# Revit family: Sideboard-Teknion-CFBTL-Figure-36h_Triple_Low_Base-R2023
name_source: partatom
category: Furniture
units: mm (PartAtom-declared; Revit-internal decimal feet)

## family parameters
Always vertical = Yes
Cut with Voids When Loaded = No
Enable Cutting in Views = No
OmniClass Number = 23.40.20.00
OmniClass Title = General Furniture and Specialties
Render Appearance Source = Family Geometry
Room Calculation Point = No
Shared = Yes
Work Plane-Based = Yes

## types (6) — shared parameters
Assembly Code = E2020200
Default Elevation = 48 "
Description = 36H Triple Sideboard, Low Base
Dim1 = 15 "
HDH = No
Height = 37 "
Manufacturer = Teknion
Manufacturer Fax = 416.661.4586
Part Number = CFBTL
Product Documentation Link = https://d2r72yk5wmppdj.cloudfront.net
Product Line = Custom Wood
Product Page URL = https://www.teknion.com
Series = Figure
Sustainability Data = https://www.teknion.com
URL = www.teknion.com
Unit Weight URL = http://www.teknion.com
Warranty = http://www.teknion.com

## per-type parameters (varying)
| type | HCH | HHH | HWH | Model | WCW | WDW |
| (HHH) All H.Doors | No | Yes | No | CFBTL_HHH | No | No |
| (HCH) H.Door/ Cutouts for AV or Fridge/ H.Door | Yes | No | No | CFBTL_HCH | No | No |
| (WCW) Waste/ Cutouts for AV or Fridge/ Waste | No | No | No | CFBTL_WCW | Yes | No |
| (HWH) H.Door/ Waste/ H.Door | No | No | Yes | CFBTL_HWH | No | No |
| (WDW) Waste/ Drawer/ Waste | No | No | No | CFBTL_WDW | No | Yes |
| (HDH) H.Door/ Drawer/ H.Door | No | No | Yes | CFBTL_HDH | No | No |

## geometry (parser evidence)
native form markers: Sweep x9
no freeform markers — native parametric forms only
